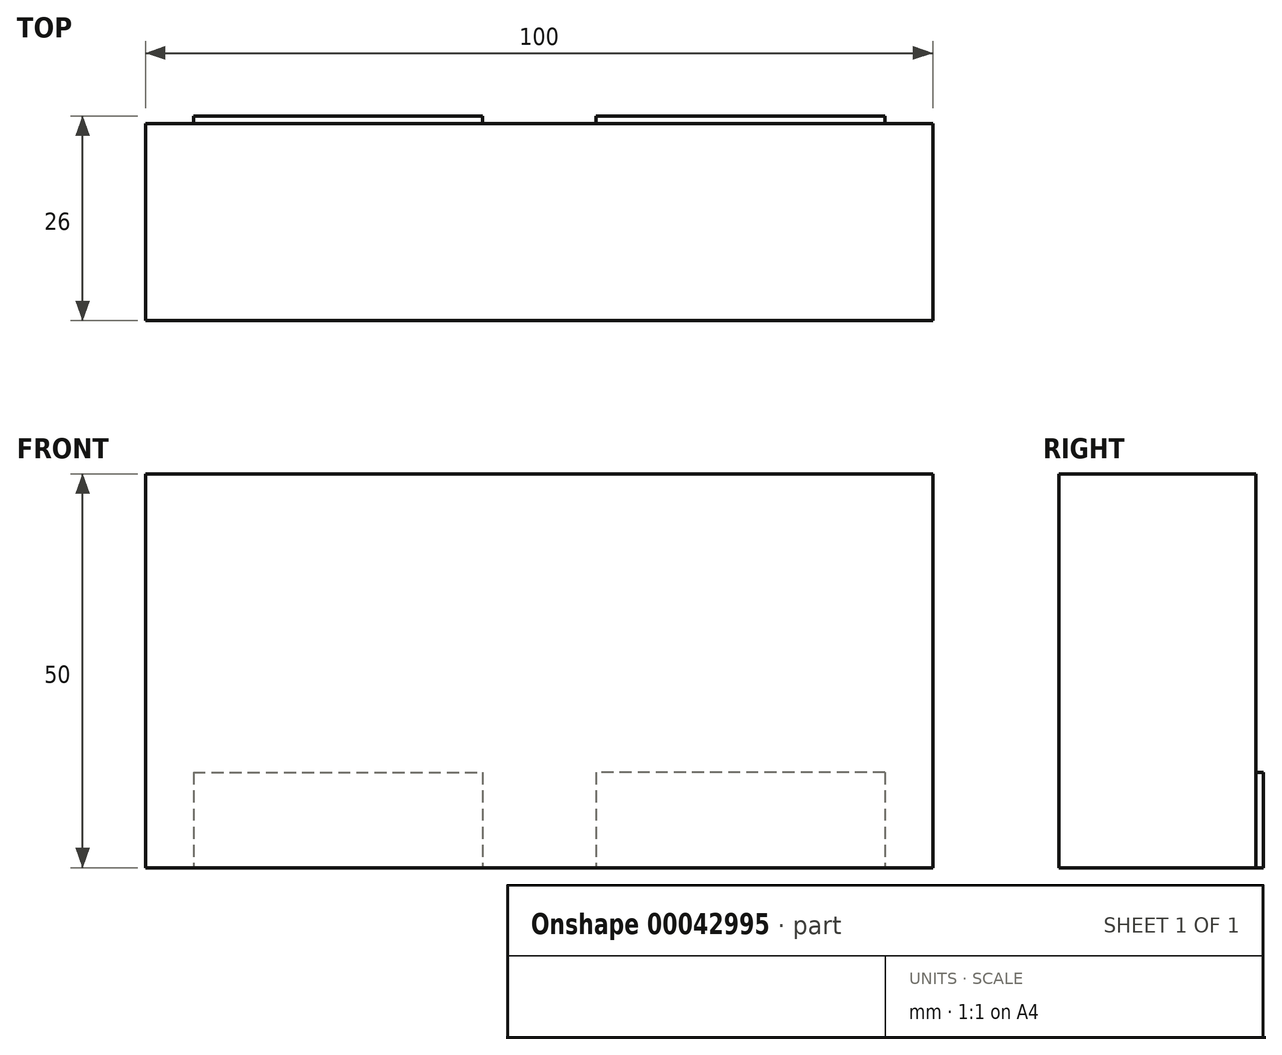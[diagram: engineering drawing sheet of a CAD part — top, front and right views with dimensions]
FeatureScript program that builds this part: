
annotation { "Feature Type Name" : "Feature", "Feature Type Description" : "" }
export const myFeature = defineFeature(function(context is Context, id is Id, definition is map)
    precondition{}
    {
        {
            var Q0;
            Q0=qCreatedBy(makeId("Front.planeOp"),FACE);
            var sketch = newSketch(context, id + "F0", { "sketchPlane" : qUnion([Q0])});
            skLineSegment(sketch, "E0", {"start": v(0, 0) * mm, "end": v(-50, 0) * mm});
            skLineSegment(sketch, "E1", {"start": v(-50, 0) * mm, "end": v(-50, 50) * mm});
            skLineSegment(sketch, "E2", {"start": v(-50, 50) * mm, "end": v(0, 50) * mm});
            skLineSegment(sketch, "E3.MirrorCS", {"start": v(50, 50) * mm, "end": v(0, 50) * mm});
            skLineSegment(sketch, "E4.MirrorCS", {"start": v(50, 0) * mm, "end": v(50, 50) * mm});
            skLineSegment(sketch, "E5.MirrorCS", {"start": v(0, 0) * mm, "end": v(50, 0) * mm});
            skSolve(sketch);
        }
        {
            var Q0;
            Q0 = qSketchRegion(id + "F0", true);
            extrude(context, id + "F1", {"entities" : qUnion([Q0]), "depth" : 25 * mm});
        }
        {
            var Q0;
            Q0=makeQuery(id+"F1.opExtrude","CAP_FACE",FACE,{"disambiguationData":[OSD([sQuery(id+"F0.wireOp",EDGE,"E0"),sQuery(id+"F0.wireOp",EDGE,"E1"),sQuery(id+"F0.wireOp",EDGE,"E2"),sQuery(id+"F0.wireOp",EDGE,"E3.MirrorCS"),sQuery(id+"F0.wireOp",EDGE,"E4.MirrorCS"),sQuery(id+"F0.wireOp",EDGE,"E5.MirrorCS")])],"isStart":true});
            var sketch = newSketch(context, id + "F2", { "sketchPlane" : qUnion([Q0])});
            skLineSegment(sketch, "E6.bottom", {"start": v(-43.92, 12.08) * mm, "end": v(-7.23, 12.08) * mm});
            skLineSegment(sketch, "E6.top", {"start": v(-43.92, 0) * mm, "end": v(-7.23, 0) * mm});
            skLineSegment(sketch, "E6.left", {"start": v(-43.92, 12.08) * mm, "end": v(-43.92, 0) * mm});
            skLineSegment(sketch, "E6.right", {"start": v(-7.23, 12.08) * mm, "end": v(-7.23, 0) * mm});
            skLineSegment(sketch, "E7.MirrorCS", {"start": v(7.23, 12.08) * mm, "end": v(7.23, 0) * mm});
            skLineSegment(sketch, "E8.MirrorCS", {"start": v(43.92, 12.08) * mm, "end": v(43.92, 0) * mm});
            skLineSegment(sketch, "E9.MirrorCS", {"start": v(43.92, 12.08) * mm, "end": v(7.23, 12.08) * mm});
            skLineSegment(sketch, "E10.MirrorCS", {"start": v(43.92, 0) * mm, "end": v(7.23, 0) * mm});
            skSolve(sketch);
        }
        {
            var Q0;
            Q0 = qSketchRegion(id + "F2", true);
            extrude(context, id + "F3", {"entities" : qUnion([Q0]), "operationType" : NewBodyOperationType.ADD, "depth" : 1 * mm});
        }
    });
